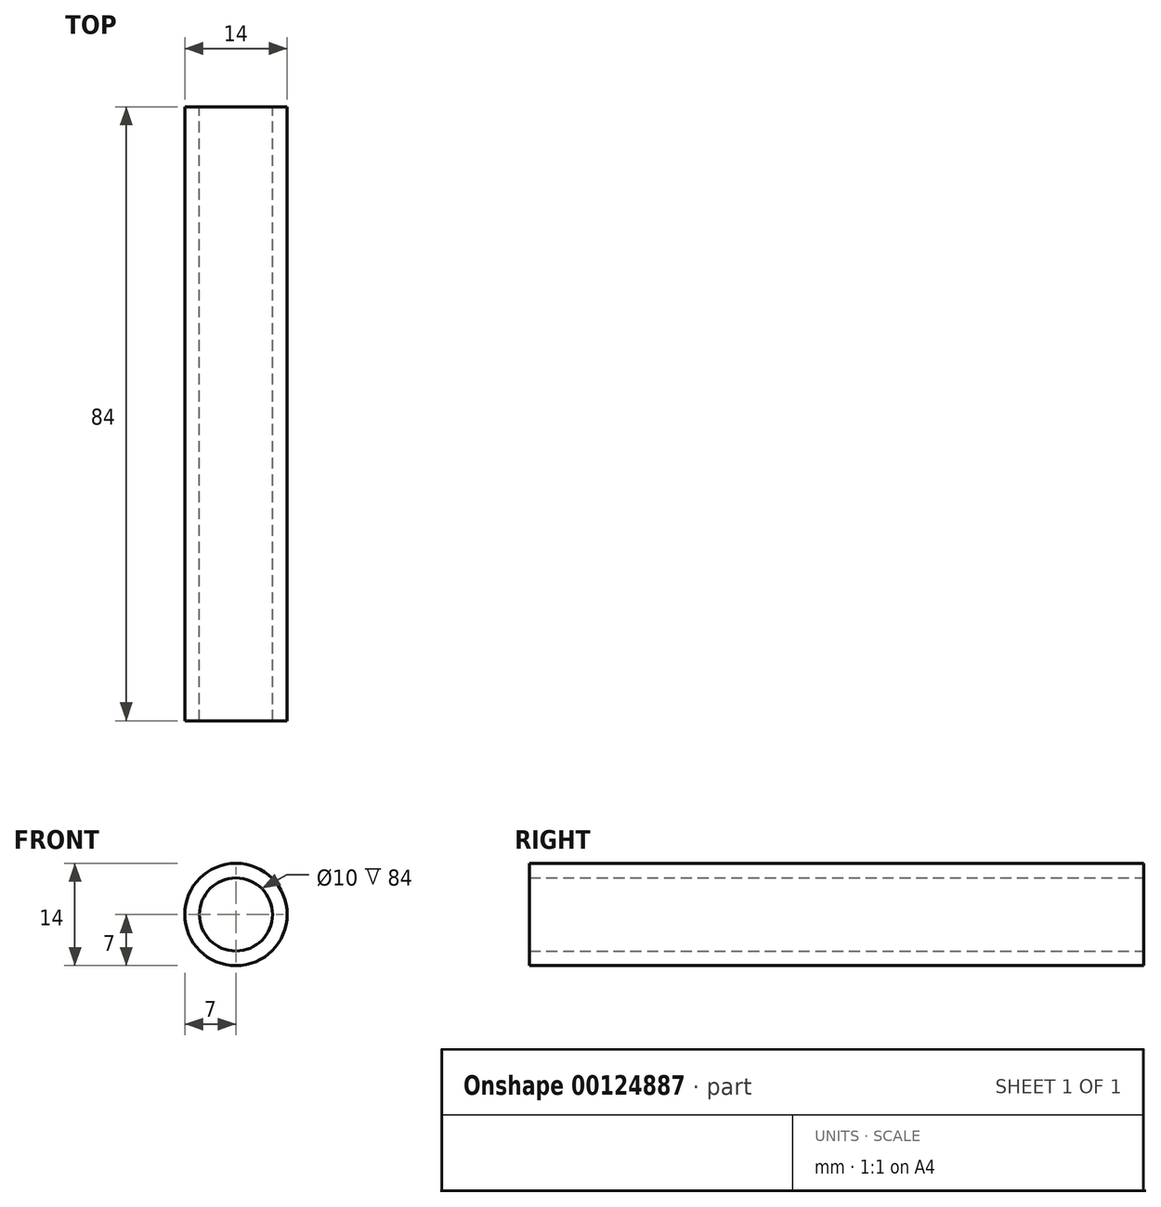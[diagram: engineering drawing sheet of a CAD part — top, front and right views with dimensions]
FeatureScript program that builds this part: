
annotation { "Feature Type Name" : "Feature", "Feature Type Description" : "" }
export const myFeature = defineFeature(function(context is Context, id is Id, definition is map)
    precondition{}
    {
        {
            var Q0;
            Q0=qCreatedBy(makeId("Front.planeOp"),FACE);
            var sketch = newSketch(context, id + "F0", { "sketchPlane" : qUnion([Q0])});
            skCircle(sketch, "E0", {"center": v(0, 0) * mm, "radius": 7 * mm});
            skCircle(sketch, "E1.0", {"center": v(0, 0) * mm, "radius": 5 * mm});
            skSolve(sketch);
        }
        {
            var Q0;
            Q0=makeQuery(id+"F0.imprint","IMPRINT",FACE,{"disambiguationData":[TD([[makeQuery(id+"F0.imprint","IMPRINT",EDGE,{"derivedFrom":sQuery(id+"F0.wireOp",EDGE,"E0")}),1.0]])]});
            extrude(context, id + "F1", {"entities" : qUnion([Q0]), "endBound" : BoundingType.SYMMETRIC, "depth" : 84 * mm});
        }
    });
